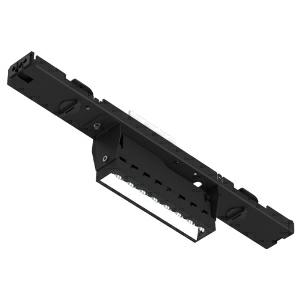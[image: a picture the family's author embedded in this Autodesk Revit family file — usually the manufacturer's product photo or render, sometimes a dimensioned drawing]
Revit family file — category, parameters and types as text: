
# Revit family: magiq_hollow_wallwash_7-01808-00
name_source: partatom
category: Lighting Fixtures
units: mm (PartAtom-declared; Revit-internal decimal feet)

## family parameters
Cut with Voids When Loaded = No
Host = Face
Light Source = No
Part Type = Normal
Room Calculation Point = No
Round Connector Dimension = Use Diameter
Shared = No

## types (1)
- 7-01808-00-H27-U02 (1 x LED, 1491.91 lm, 18.7 W, 2700K)
    Apparent Load = 19 VA
    CIE Flux Codes = 57 81 96 100 85
    Color Rendering = 1A/90…99
    Color Temperature = 2700K
    Default Elevation = 1800 mm
    Description = MAGIQ HOLLOW WALLWASH
    Height = 0 mm  [stored 0 ft]
    Lamp = 1 x LED
    Lamp Light Flux = 1491.91 lm
    Lamp Power = 18.7 W
    Lamp count = 1
    Length = 450 mm
    Luminous efficacy = 68 lm/W
    Manufacturer = Prolicht
    ModVariant = No
    Model = 7-01808-00
    Mounting Place = Ceiling
    Mounting Type = Recessed
    Number of Poles = 1
    OnlyDefault = Yes
    Power Factor = 1
    Product Name = MAGIQ HOLLOW WALLWASH
    Product group = Trimless recessed spotlights
    ProductGroupID = 412
    Protection Class = Protection class
    Protection Degree = Degree of protection
    RLX_Detail_Level = 1
    RlxData = <blob elided: 321325 chars, md5=d7c3b105>
    Socket = socket
    Standby Power = 0 W
    System Light Flux = 1270 lm
    System Power = 19 W
    Type Comments = LED COLOUR DIR 2700 K (27),FRAME_COLOUR BLACK (02)
    Type Image = 7-01808-00.jpg
    URL = http://relux.com
    VarID = 7-01808-00-h27-u02
    Voltage = 0 V
    Weight = 0.00 kg
    Width = 49 mm

note: [stored X ft] marks values corroborated as IEEE doubles in the binary element streams (Revit-internal decimal feet)

## geometry (parser evidence)
native form markers: Blend x4, Sweep x12
no freeform markers — native parametric forms only
